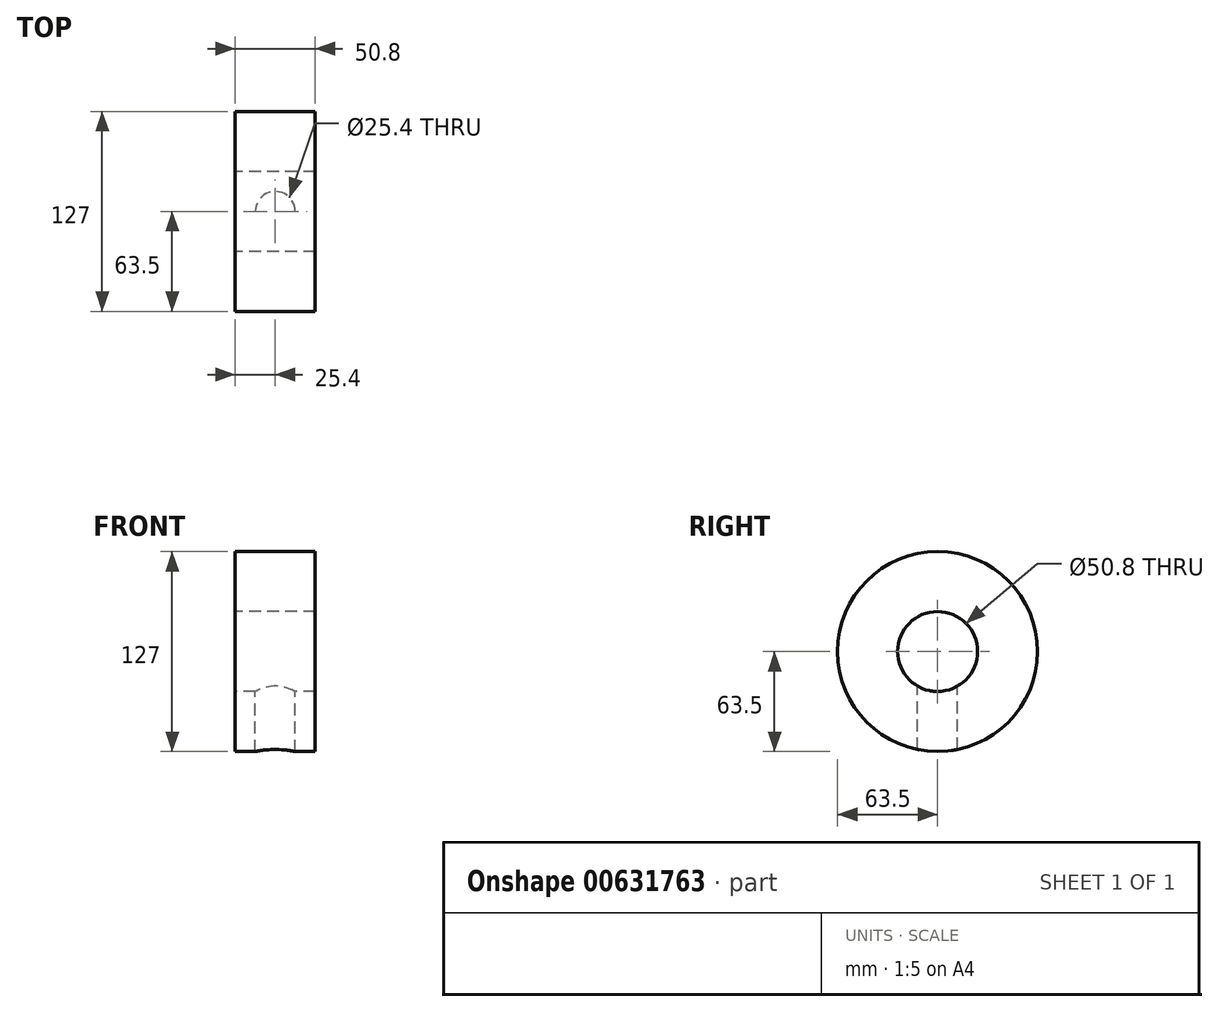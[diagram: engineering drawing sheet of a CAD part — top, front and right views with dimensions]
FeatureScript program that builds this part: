
annotation { "Feature Type Name" : "Feature", "Feature Type Description" : "" }
export const myFeature = defineFeature(function(context is Context, id is Id, definition is map)
    precondition{}
    {
        {
            var Q0;
            Q0=qCreatedBy(makeId("Right.planeOp"),FACE);
            var sketch = newSketch(context, id + "F0", { "sketchPlane" : qUnion([Q0])});
            skCircle(sketch, "E0", {"center": v(0, 0) * mm, "radius": 63.5 * mm});
            skSolve(sketch);
        }
        {
            var Q0;
            Q0=makeQuery(id+"F0.imprint","IMPRINT",FACE,{"disambiguationData":[TD([[makeQuery(id+"F0.imprint","IMPRINT",EDGE,{"derivedFrom":sQuery(id+"F0.wireOp",EDGE,"E0")}),1.0]])]});
            extrude(context, id + "F1", {"entities" : qUnion([Q0]), "endBound" : BoundingType.SYMMETRIC, "depth" : 50.8 * mm, "offsetDistance" : 25.4 * mm});
        }
        {
            var Q0;
            Q0=qCreatedBy(makeId("Top.planeOp"),FACE);
            var sketch = newSketch(context, id + "F2", { "sketchPlane" : qUnion([Q0])});
            skCircle(sketch, "E1", {"center": v(0, 0) * mm, "radius": 12.7 * mm});
            skSolve(sketch);
        }
        {
            var Q0;
            Q0 = qSketchRegion(id + "F2", true);
            extrude(context, id + "F3", {"entities" : qUnion([Q0]), "operationType" : NewBodyOperationType.REMOVE, "oppositeDirection" : true, "depth" : 76.2 * mm, "offsetDistance" : 25.4 * mm});
        }
        {
            var Q0;
            Q0=qCreatedBy(makeId("Right.planeOp"),FACE);
            var sketch = newSketch(context, id + "F4", { "sketchPlane" : qUnion([Q0])});
            skCircle(sketch, "E2", {"center": v(0, 0) * mm, "radius": 25.4 * mm});
            skSolve(sketch);
        }
        {
            var Q0;
            Q0 = qSketchRegion(id + "F4", true);
            extrude(context, id + "F5", {"entities" : qUnion([Q0]), "operationType" : NewBodyOperationType.REMOVE, "endBound" : BoundingType.SYMMETRIC, "depth" : 63.5 * mm, "offsetDistance" : 25.4 * mm});
        }
    });
